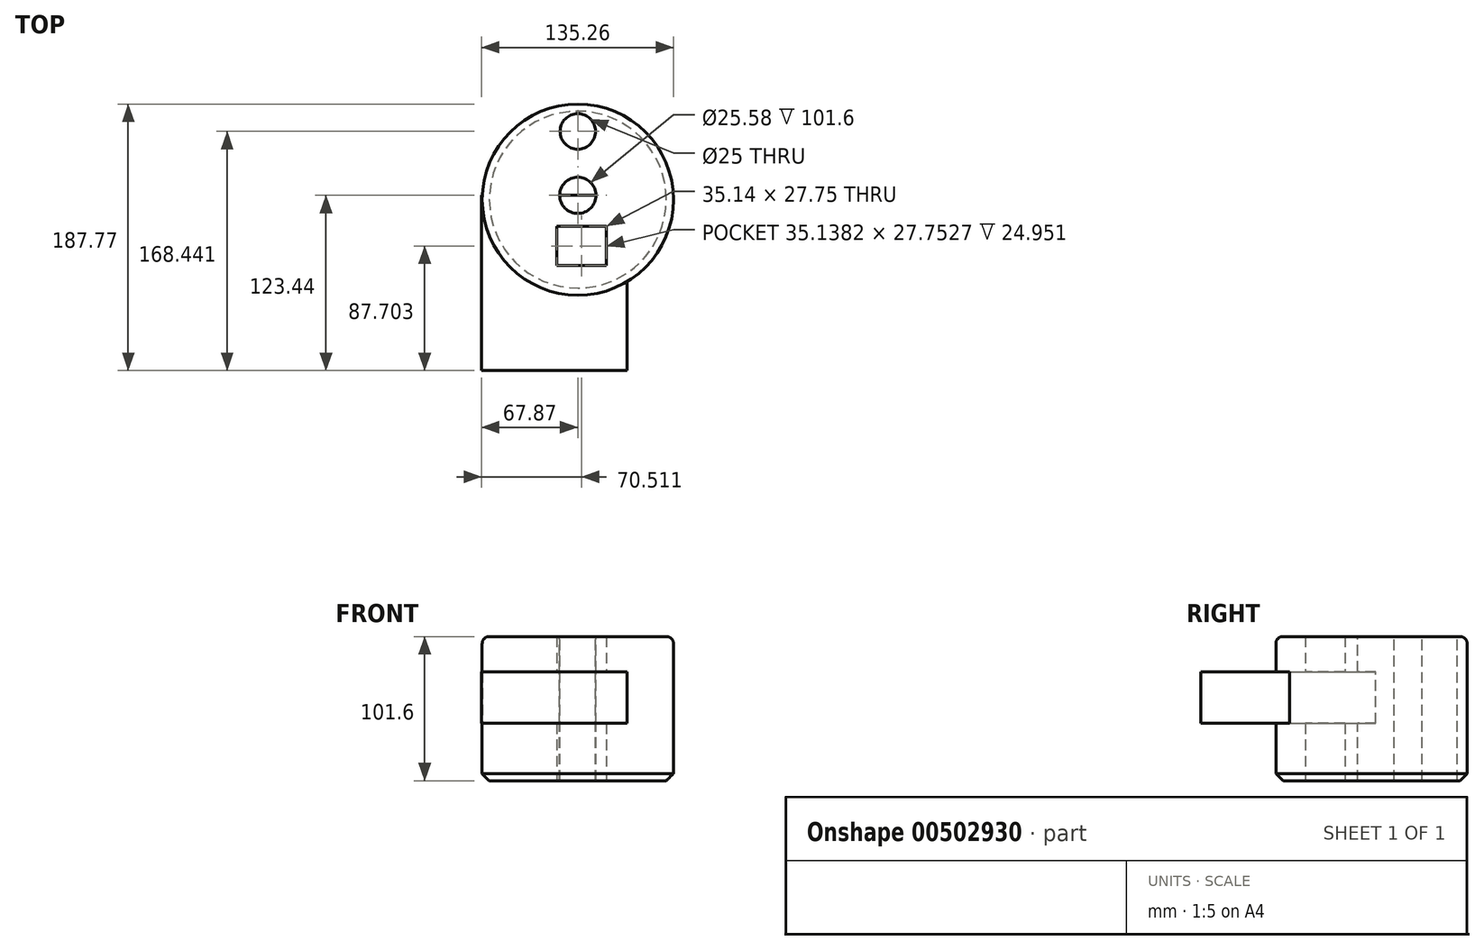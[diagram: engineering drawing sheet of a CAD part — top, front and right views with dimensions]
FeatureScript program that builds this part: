
annotation { "Feature Type Name" : "Feature", "Feature Type Description" : "" }
export const myFeature = defineFeature(function(context is Context, id is Id, definition is map)
    precondition{}
    {
        {
            var Q0;
            Q0=qCreatedBy(makeId("Top.planeOp"),FACE);
            var sketch = newSketch(context, id + "F0", { "sketchPlane" : qUnion([Q0])});
            skCircle(sketch, "E0", {"center": v(0, -3.06) * mm, "radius": 67.39 * mm});
            skSolve(sketch);
        }
        {
            var Q0;
            Q0=makeQuery(id+"F0.imprint","IMPRINT",FACE,{"disambiguationData":[TD([[makeQuery(id+"F0.imprint","IMPRINT",EDGE,{"derivedFrom":sQuery(id+"F0.wireOp",EDGE,"E0")}),1.0]])]});
            extrude(context, id + "F1", {"entities" : qUnion([Q0]), "depth" : 101.6 * mm});
        }
        {
            var Q0;
            Q0=makeQuery(id+"F1.opExtrude","CAP_FACE",FACE,{"disambiguationData":[OSD([sQuery(id+"F0.wireOp",EDGE,"E0")])],"isStart":false});
            var sketch = newSketch(context, id + "F2", { "sketchPlane" : qUnion([Q0])});
            skCircle(sketch, "E1", {"center": v(0, 0) * mm, "radius": 12.79 * mm});
            skSolve(sketch);
        }
        {
            var Q0;
            Q0 = qSketchRegion(id + "F2", true);
            extrude(context, id + "F3", {"entities" : qUnion([Q0]), "operationType" : NewBodyOperationType.REMOVE, "oppositeDirection" : true, "depth" : 161.8 * mm});
        }
        {
            var Q0;
            Q0=makeQuery(id+"F1.opExtrude","CAP_FACE",FACE,{"disambiguationData":[OSD([sQuery(id+"F0.wireOp",EDGE,"E0")])],"isStart":false});
            var sketch = newSketch(context, id + "F4", { "sketchPlane" : qUnion([Q0])});
            skCircle(sketch, "E2", {"center": v(0, 45) * mm, "radius": 12.5 * mm});
            skSolve(sketch);
        }
        {
            var Q0;
            Q0=makeQuery(id+"F4.imprint","IMPRINT",FACE,{"disambiguationData":[TD([[makeQuery(id+"F4.imprint","IMPRINT",EDGE,{"derivedFrom":sQuery(id+"F4.wireOp",EDGE,"E2")}),1.0]])]});
            extrude(context, id + "F5", {"entities" : qUnion([Q0]), "operationType" : NewBodyOperationType.REMOVE, "oppositeDirection" : true, "depth" : 121.67 * mm});
        }
        {
            var Q0;
            Q0=makeQuery(id+"F1.opExtrude","CAP_EDGE",EDGE,{"disambiguationData":[OSD([sQuery(id+"F0.wireOp",EDGE,"E0")])],"isStart":false});
            fillet(context, id + "F6", {"entities" : qUnion([Q0]), "radius" : 5.08 * mm, "tangentPropagation" : true, "allowEdgeOverflow" : false});
        }
        {
            var Q0;
            Q0=makeQuery(id+"F1.opExtrude","CAP_EDGE",EDGE,{"disambiguationData":[OSD([sQuery(id+"F0.wireOp",EDGE,"E0")])],"isStart":true});
            chamfer(context, id + "F7", {"entities" : qUnion([Q0]), "width" : 5.08 * mm, "tangentPropagation" : true});
        }
        {
            var Q0;
            Q0=makeQuery(id+"F1.opExtrude","CAP_FACE",FACE,{"disambiguationData":[OSD([sQuery(id+"F0.wireOp",EDGE,"E0")])],"isStart":true});
            var sketch = newSketch(context, id + "F8", { "sketchPlane" : qUnion([Q0])});
            skLineSegment(sketch, "E3.bottom", {"start": v(-14.93, 49.61) * mm, "end": v(20.21, 49.61) * mm});
            skLineSegment(sketch, "E3.top", {"start": v(-14.93, 21.86) * mm, "end": v(20.21, 21.86) * mm});
            skLineSegment(sketch, "E3.left", {"start": v(-14.93, 49.61) * mm, "end": v(-14.93, 21.86) * mm});
            skLineSegment(sketch, "E3.right", {"start": v(20.21, 49.61) * mm, "end": v(20.21, 21.86) * mm});
            skSolve(sketch);
        }
        {
            var Q0;
            Q0 = qSketchRegion(id + "F8", true);
            extrude(context, id + "F9", {"entities" : qUnion([Q0]), "operationType" : NewBodyOperationType.REMOVE, "oppositeDirection" : true, "depth" : 223.27 * mm});
        }
        {
            var Q0;
            Q0=qCreatedBy(makeId("Front.planeOp"),FACE);
            var sketch = newSketch(context, id + "F10", { "sketchPlane" : qUnion([Q0])});
            skLineSegment(sketch, "E4.bottom", {"start": v(34.57, 40.4) * mm, "end": v(-67.87, 40.4) * mm});
            skLineSegment(sketch, "E4.top", {"start": v(34.57, 76.65) * mm, "end": v(-67.87, 76.65) * mm});
            skLineSegment(sketch, "E4.left", {"start": v(34.57, 40.4) * mm, "end": v(34.57, 76.65) * mm});
            skLineSegment(sketch, "E4.right", {"start": v(-67.87, 40.4) * mm, "end": v(-67.87, 76.65) * mm});
            skSolve(sketch);
        }
        {
            var Q0;
            Q0 = qSketchRegion(id + "F10", true);
            extrude(context, id + "F11", {"entities" : qUnion([Q0]), "operationType" : NewBodyOperationType.ADD, "depth" : 25.4 * mm});
        }
        {
            var Q0;
            Q0 = qSketchRegion(id + "F10", true);
            extrude(context, id + "F12", {"entities" : qUnion([Q0]), "operationType" : NewBodyOperationType.ADD, "depth" : 123.44 * mm});
        }
    });
